# Revit family: RN 90015 Optifitt-Serra-Kreuz
name_source: partatom
category: Rohrformteile
units: mm (PartAtom-declared; Revit-internal decimal feet)

## family parameters
Arbeitsebenenbasiert = Nein
Beim Laden mit Abzugskörper schneiden = Nein
Bemaßung runder Anschluss = Durchmesser verwenden
Gemeinsam genutzt = Nein
Immer vertikal = Ja
Teiletyp = Kreuzstück

## types (3) — shared parameters
1.010.00.2 Blattnummer der Richtlinie = 29
1.010.00.3 Ausgabedatum (Monat) der Richtlinie = 201308
1.010.00.4 Herstellername = R. Nussbaum AG
1.010.00.5 Revisionsdatum der Datei = 20190521
1.010.00.6 Webadresse des Herstellers = http://www.nussbaum.ch
1.100.00.4 Produktbezeichnung = Versorgung
1.110.00.2 Index = 3
1.110.00.4 Produktbezeichnung = Optifitt-Serra
1.960/3L.00.8 Link (URL) = https://www.nussbaum.ch
29.700.00.4 Produktname = Optifitt-Serra-Kreuz
29.700.00.5 Produktkennung = 2
29.700.00.6 Querschnittsform = 1
29.700.00.7 Nennweitensystem = DN
29.700.00.8 Nenndrucksystem = PN
29.710.02.4 Nenndruck = 16
29.710.02.5 max. zul. Überdruck [hPa] = 1600
29.710.02.7 max. zul. Dauer-Betriebsdruck [hPa] = 1600
29.710.02.9 max. zul. Dauer-Betriebstemperatur [°C] = 90
CONNECTOR2_DIAMETER_dY_0r = 15 mm
CONNECTOR2_dY_00 = 27 mm
CONNECTOR2_dY_01 = 14 mm  [stored 0.0459318 ft]
CONNECTOR2_ref_dY = 14 mm  [stored 0.0459318 ft]
CONNECTOR3_DIAMETER_dX_0r = 15 mm
CONNECTOR3_dX_00 = 27 mm
CONNECTOR3_dX_01 = 14 mm  [stored 0.0459318 ft]
CONNECTOR3_ref_dX = 14 mm  [stored 0.0459318 ft]
Connector Visibility = Nein
EnclosingSpace Visibility = Nein
Hersteller = R. Nussbaum AG
URL = https://www.nussbaum.ch

## per-type parameters (varying)
| type | 1.800.00.3 TGA-Nummer | 1.800.00.4 Kommentarfeld | 1.810.00.3 Hersteller-Bestellnummer | 1.810.00.4 DATANORM-Nummer | 1.810.00.5 StLB-Nummer | 1.810.00.6 GTIN-Nummer | 29.710.02.10 Formstück-Gewicht [kg] | 29.710.02.3 Benennung | CONNECTOR0_DIAMETER_dX_0r | CONNECTOR0_dX_00 | CONNECTOR0_dX_01 | CONNECTOR0_ref_dX | CONNECTOR1_DIAMETER_dY_0r | CONNECTOR1_dY_00 | CONNECTOR1_dY_01 | CONNECTOR1_ref_dY | Modell | R. Nussbaum AG 90015.04 de Visibility | R. Nussbaum AG 90015.05 de Visibility | R. Nussbaum AG 90015.06 de Visibility | Typenkommentare |
| DN=25 | 01900300000000000000000000000000000000000000000009000000000000000003 | 90015.06, Optifitt-Serra-Kreuz, DN=25, L=38, Rp=1 | 90015.06 | 90015.06 | 213.814 | 7612945033086 | 0.376 | Optifitt-Serra-Kreuz, DN=25, L=38, Rp=1 | 25 mm  [stored 0.082021 ft] | 21 mm | 38 mm | 21 mm | 25 mm  [stored 0.082021 ft] | 21 mm | 38 mm | 21 mm | 90015.06 | Nein | Nein | Ja | Optifitt-Serra-Kreuz DN=25 |
| DN=20 | 01900300000000000000000000000000000000000000000009000000000000000002 | 90015.05, Optifitt-Serra-Kreuz, DN=20, L=32, Rp=¾ | 90015.05 | 90015.05 | 213.813 | 7612945033079 | 0.235 | Optifitt-Serra-Kreuz, DN=20, L=32, Rp=¾ | 20 mm | 17 mm | 32 mm | 17 mm | 20 mm | 17 mm | 32 mm | 17 mm | 90015.05 | Nein | Ja | Nein | Optifitt-Serra-Kreuz DN=20 |
| DN=15 | 01900300000000000000000000000000000000000000000009000000000000000001 | 90015.04, Optifitt-Serra-Kreuz, DN=15, L=27, Rp=½ | 90015.04 | 90015.04 | 213.812 | 7612945033062 | 0.145 | Optifitt-Serra-Kreuz, DN=15, L=27, Rp=½ | 15 mm | 14 mm  [stored 0.0459318 ft] | 27 mm | 14 mm  [stored 0.0459318 ft] | 15 mm | 14 mm  [stored 0.0459318 ft] | 27 mm | 14 mm  [stored 0.0459318 ft] | 90015.04 | Ja | Nein | Nein | Optifitt-Serra-Kreuz DN=15 |

note: [stored X ft] marks values corroborated as IEEE doubles in the binary element streams (Revit-internal decimal feet)

## geometry (parser evidence)
native form markers: Sweep x2
no freeform markers — native parametric forms only
